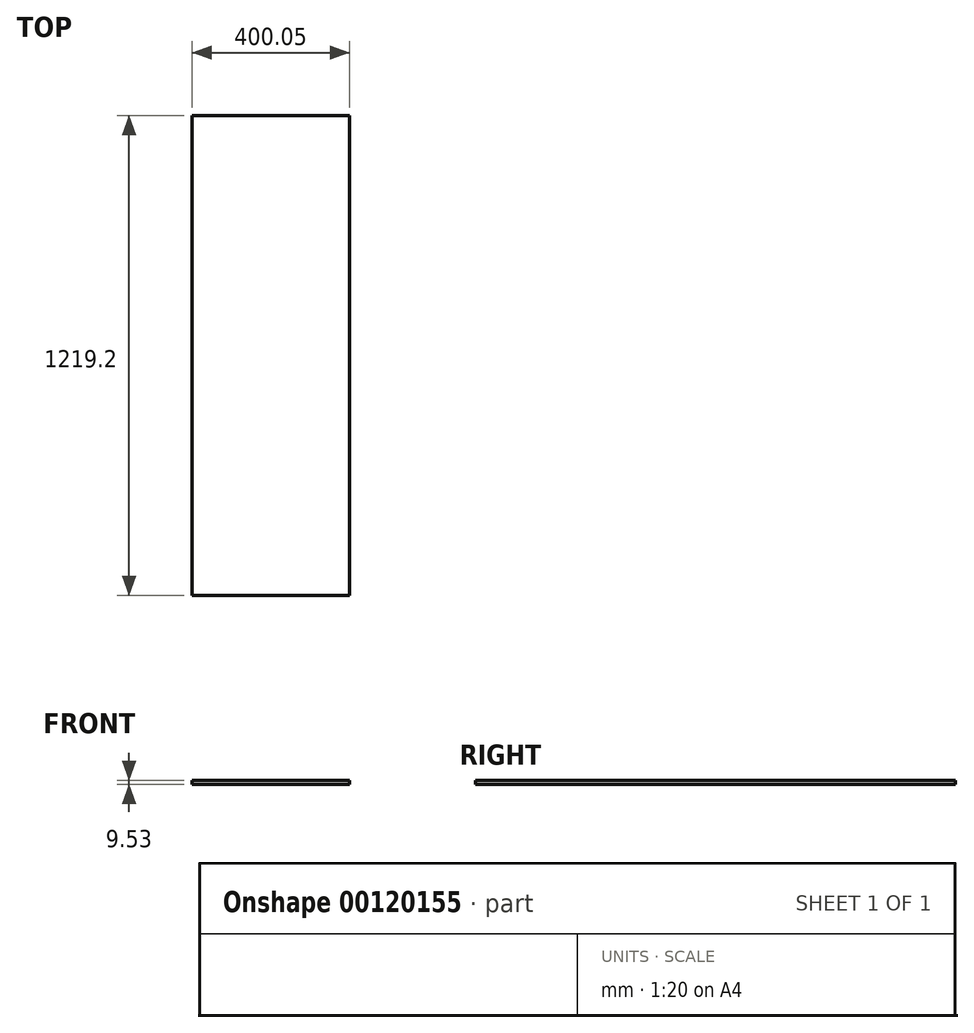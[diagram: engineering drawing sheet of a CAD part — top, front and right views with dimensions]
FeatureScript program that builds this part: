
annotation { "Feature Type Name" : "Feature", "Feature Type Description" : "" }
export const myFeature = defineFeature(function(context is Context, id is Id, definition is map)
    precondition{}
    {
        {
            var Q0;
            Q0=qCreatedBy(makeId("Front.planeOp"),FACE);
            var sketch = newSketch(context, id + "F0", { "sketchPlane" : qUnion([Q0])});
            skLineSegment(sketch, "E0", {"start": v(-39.2, -12.58) * mm, "end": v(-39.2, -3.05) * mm});
            skLineSegment(sketch, "E1", {"start": v(-39.2, -3.05) * mm, "end": v(360.86, -3.05) * mm});
            skLineSegment(sketch, "E2", {"start": v(360.86, -3.05) * mm, "end": v(360.86, -12.58) * mm});
            skLineSegment(sketch, "E3", {"start": v(360.86, -12.58) * mm, "end": v(-39.2, -12.58) * mm});
            skSolve(sketch);
        }
        {
            var Q0;
            Q0=makeQuery(id+"F0.imprint","IMPRINT",FACE,{"disambiguationData":[TD([[makeQuery(id+"F0.imprint","IMPRINT",EDGE,{"derivedFrom":sQuery(id+"F0.wireOp",EDGE,"E0")}),-1.0]])]});
            extrude(context, id + "F1", {"entities" : qUnion([Q0]), "depth" : 1219.2 * mm});
        }
    });
